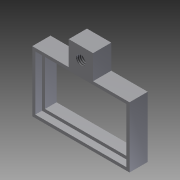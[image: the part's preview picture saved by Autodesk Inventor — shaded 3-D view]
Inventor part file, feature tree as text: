
AUTODESK INVENTOR PART (.ipt)
format: ipt  version: 2011 (Build 150239000, 239)  size: 116,736 bytes
history: native  units: in
note: dims shown in document units (in); Inventor stores cm internally (conversion verified against a paired STEP export)
features: sketch x5, extrude x4, hole x1, thread x1
ambient origin geometry x8: Origin, YZ Plane, XZ Plane, XY Plane, X Axis, Y Axis, Z Axis, Center Point
bodies: Solid1 (feature_tree)
feature tree (11):
  extrude  "Extrusion1"  Depth=0.3937in
  extrude  "Extrusion2"  Depth=0.5512in
  extrude  "Extrusion3"  Depth=0.1181in TaperAngle=0.0deg
  extrude  "Extrusion4"  Depth=0.2362in
  hole  "Hole1"  [1 undecoded]
  thread  "Thread1"  [1 undecoded]
  sketch  "Sketch1"  dims[d0=0.6299in d1=0.3937in]
  sketch  "Sketch2"  dims[d2=0.1181in d3=0.0in d4=0.5512in]
  sketch  "Sketch3"  dims[d5=0.315in d6=0.1181in d7=0.0in]
  sketch  "Sketch5"  dims[d13=0.1575in d14=0.2362in]
  sketch  "Sketch6"  dims[d15=0.1575in d16=0.0in d17=0.0197in d18=0.0433in d19=0.0in d20=0.06in d21=0.75in d22=0.375in d23=0.25in d24=0.5635in d25=0.07in d26=0.8108in d27=1.0in d28=0.0in]
note: 2 required parameter values undecoded (feature->parameter linkage not recoverable at this tier; creation-order binding heuristic only, values carry confidence <= 0.55)
